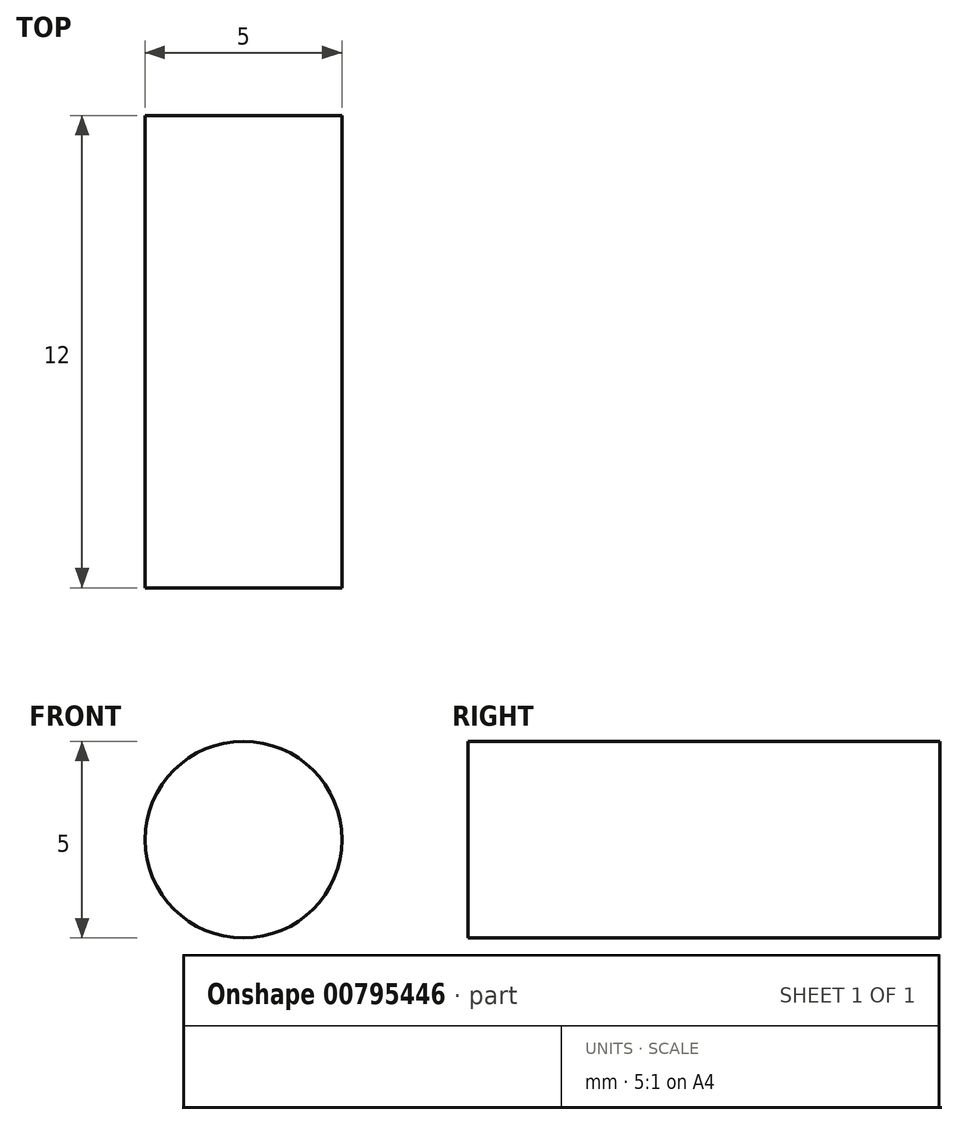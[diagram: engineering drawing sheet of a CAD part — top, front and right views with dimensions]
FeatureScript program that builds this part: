
annotation { "Feature Type Name" : "Feature", "Feature Type Description" : "" }
export const myFeature = defineFeature(function(context is Context, id is Id, definition is map)
    precondition{}
    {
        {
            var Q0;
            Q0=qCreatedBy(makeId("Front.planeOp"),FACE);
            var sketch = newSketch(context, id + "F0", { "sketchPlane" : qUnion([Q0])});
            skCircle(sketch, "E0", {"center": v(0, 0) * mm, "radius": 2.5 * mm});
            skSolve(sketch);
        }
        {
            var Q0;
            Q0=makeQuery(id+"F0.imprint","IMPRINT",FACE,{"disambiguationData":[TD([[makeQuery(id+"F0.imprint","IMPRINT",EDGE,{"derivedFrom":sQuery(id+"F0.wireOp",EDGE,"E0")}),1.0]])]});
            extrude(context, id + "F1", {"entities" : qUnion([Q0]), "depth" : 72 * mm, "offsetDistance" : 25 * mm});
        }
        {
            var Q0;
            Q0=makeQuery(id+"F1.opExtrude","CAP_FACE",FACE,{"disambiguationData":[OSD([sQuery(id+"F0.wireOp",EDGE,"E0")])],"isStart":false});
            extrude(context, id + "F2", {"entities" : qUnion([Q0]), "operationType" : NewBodyOperationType.REMOVE, "oppositeDirection" : true, "depth" : 50 * mm, "offsetDistance" : 25 * mm});
        }
        {
            var Q0;
            Q0=makeQuery(id+"F2.boolean.opBoolean","COPY",FACE,{"derivedFrom":makeQuery(id+"F2.opExtrude","CAP_FACE",FACE,{"disambiguationData":[OSD([sQuery(id+"F0.wireOp",EDGE,"E0")])],"isStart":false})});
            extrude(context, id + "F3", {"entities" : qUnion([Q0]), "operationType" : NewBodyOperationType.REMOVE, "oppositeDirection" : true, "depth" : 10 * mm, "offsetDistance" : 25 * mm});
        }
    });
